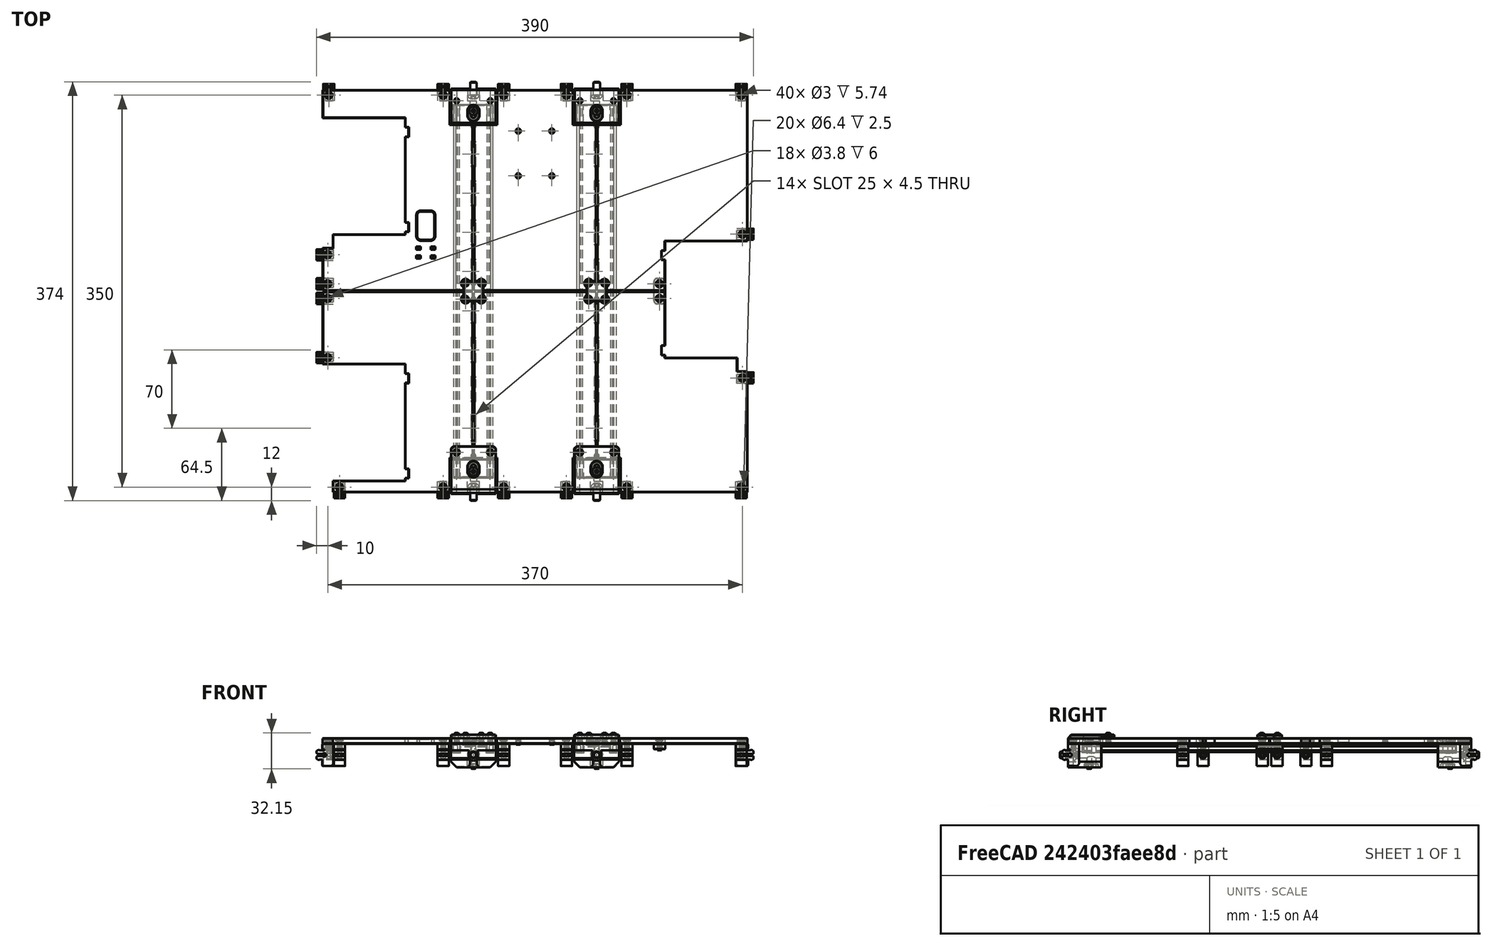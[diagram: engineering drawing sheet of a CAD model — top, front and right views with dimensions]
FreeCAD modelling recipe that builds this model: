
FCSTD DOCUMENT  (FreeCAD 0.19R24291 (Git))
Label: bottom-panel-250-assembly
License: Other
LicenseURL: GPL3
objects: Part::FeaturePython×84, Part::Feature×37, App::Part×5
note: 121 computed .brp shape members not serialized (recipe doc carries the construction recipe); baked Part::Feature solids carry a one-line shape summary decoded from their .brp

FEATURE [Part::Feature] Pocket003005  label="panel-mounter_D001"
  Placement = pos=(-179.5,-180,-10) rot=(0.57735,0.57735,0.57735;2.0944rad)
  shape: bbox 10 x 15 x 20 mm, 54 faces (baked)
FEATURE [Part::Feature] Pocket003006  label="panel-mounter_D002"
  Placement = pos=(-87,-180,-10) rot=(0.57735,0.57735,0.57735;2.0944rad)
  shape: bbox 10 x 15 x 20 mm, 54 faces (baked)
FEATURE [Part::Feature] Pocket003007  label="panel-mounter_D003"
  Placement = pos=(-33,-180,-10) rot=(0.57735,0.57735,0.57735;2.0944rad)
  shape: bbox 10 x 15 x 20 mm, 54 faces (baked)
FEATURE [Part::Feature] Pocket003008  label="panel-mounter_D004"
  Placement = pos=(23,-180,-10) rot=(0.57735,0.57735,0.57735;2.0944rad)
  shape: bbox 10 x 15 x 20 mm, 54 faces (baked)
FEATURE [Part::Feature] Pocket003009  label="panel-mounter_D005"
  Placement = pos=(77,-180,-10) rot=(0.57735,0.57735,0.57735;2.0944rad)
  shape: bbox 10 x 15 x 20 mm, 54 faces (baked)
FEATURE [Part::Feature] Pocket003010  label="panel-mounter_D006"
  Placement = pos=(179,-180,-10) rot=(0.57735,0.57735,0.57735;2.0944rad)
  shape: bbox 10 x 15 x 20 mm, 54 faces (baked)
FEATURE [Part::Feature] Pocket003011  label="panel-mounter_U001"
  Placement = pos=(-179,180,-10) rot=(0.57735,-0.57735,-0.57735;2.0944rad)
  shape: bbox 10 x 15 x 20 mm, 54 faces (baked)
FEATURE [Part::Feature] Pocket003012  label="panel-mounter_U002"
  Placement = pos=(-77,180,-10) rot=(0.57735,-0.57735,-0.57735;2.0944rad)
  shape: bbox 10 x 15 x 20 mm, 54 faces (baked)
FEATURE [Part::Feature] Pocket003013  label="panel-mounter_U003"
  Placement = pos=(-23,180,-10) rot=(0.57735,-0.57735,-0.57735;2.0944rad)
  shape: bbox 10 x 15 x 20 mm, 54 faces (baked)
FEATURE [Part::Feature] Pocket003014  label="panel-mounter_U004"
  Placement = pos=(33,180,-10) rot=(0.57735,-0.57735,-0.57735;2.0944rad)
  shape: bbox 10 x 15 x 20 mm, 54 faces (baked)
FEATURE [Part::Feature] Pocket003015  label="panel-mounter_U005"
  Placement = pos=(87,180,-10) rot=(0.57735,-0.57735,-0.57735;2.0944rad)
  shape: bbox 10 x 15 x 20 mm, 54 faces (baked)
FEATURE [Part::Feature] Pocket003016  label="panel-mounter_U006"
  Placement = pos=(189,180,-10) rot=(0.57735,-0.57735,-0.57735;2.0944rad)
  shape: bbox 10 x 15 x 20 mm, 54 faces (baked)
FEATURE [Part::Feature] Pocket003017  label="panel-mounter_L001"
  Placement = pos=(-190,37.4,-10) rot=(1,0,0;1.5708rad)
  shape: bbox 15 x 10 x 20 mm, 54 faces (baked)
FEATURE [Part::Feature] Pocket003018  label="panel-mounter_L002"
  Placement = pos=(-190,11.6,-10) rot=(1,0,0;1.5708rad)
  shape: bbox 15 x 10 x 20 mm, 54 faces (baked)
FEATURE [Part::Feature] Pocket003019  label="panel-mounter_L003"
  Placement = pos=(-190,-1.5,-10) rot=(1,0,0;1.5708rad)
  shape: bbox 15 x 10 x 20 mm, 54 faces (baked)
FEATURE [Part::Feature] Pocket003020  label="panel-mounter_L004"
  Placement = pos=(-190,-54.4,-10) rot=(1,0,0;1.5708rad)
  shape: bbox 15 x 10 x 20 mm, 54 faces (baked)
FEATURE [Part::Feature] Pocket003021  label="panel-mounter_R001"
  Placement = pos=(190,45.9,-10) rot=(0,0.707107,0.707107;3.14159rad)
  shape: bbox 15 x 10 x 20 mm, 54 faces (baked)
FEATURE [Part::Feature] Pocket003022  label="panel-mounter_R002"
  Placement = pos=(190,-82.5,-10) rot=(0,0.707107,0.707107;3.14159rad)
  shape: bbox 15 x 10 x 20 mm, 54 faces (baked)
FEATURE [Part::Feature] Cut002015026005020007004001  label="center-panel-connector"
  Placement = pos=(-55,0,5) rot=(0,0,1;0rad)
  shape: bbox 22 x 22 x 3 mm, 24 faces (baked)
FEATURE [Part::Feature] Cut002015026005020007004002  label="center-panel-connector001"
  Placement = pos=(55,0,5) rot=(0,0,1;0rad)
  shape: bbox 22 x 22 x 3 mm, 24 faces (baked)
FEATURE [Part::Feature] Chamfer003004002  label="bottom-din-holder"
  Placement = pos=(-55,-165,-25) rot=(0,0,1;3.14159rad)
  shape: bbox 40 x 31 x 21 mm, 75 faces (baked)
FEATURE [Part::Feature] Chamfer003004003  label="bottom-din-holder001"
  Placement = pos=(55,-165,-25) rot=(0,0,1;3.14159rad)
  shape: bbox 40 x 31 x 21 mm, 75 faces (baked)
FEATURE [Part::Feature] Chamfer003004004  label="bottom-din-holder002"
  Placement = pos=(55,165,-25) rot=(0,0,1;0rad)
  shape: bbox 40 x 31 x 21 mm, 75 faces (baked)
FEATURE [Part::Feature] Chamfer003004005  label="bottom-din-holder003"
  Placement = pos=(-55,165,-25) rot=(0,0,1;0rad)
  shape: bbox 40 x 31 x 21 mm, 75 faces (baked)
FEATURE [Part::Feature] Cut001001  label="front-din-cap"
  Placement = pos=(-55,-165,0) rot=(0,0,1;0rad)
  shape: bbox 40 x 41.5 x 9 mm, 50 faces (baked)
FEATURE [Part::Feature] Chamfer005007002029002004001  label="back-din-cap"
  Placement = pos=(-55,165,-25) rot=(0,0,1;0rad)
  shape: bbox 40 x 30 x 6 mm, 55 faces (baked)
FEATURE [Part::Feature] Chamfer005007002029002004002  label="back-din-cap001"
  Placement = pos=(55,165,-25) rot=(0,0,1;0rad)
  shape: bbox 40 x 30 x 6 mm, 55 faces (baked)
FEATURE [Part::Feature] Cut002015026005020007004003  label="front-din-cap001"
  Placement = pos=(55,-165,0) rot=(0,0,1;0rad)
  shape: bbox 40 x 41.5 x 9 mm, 50 faces (baked)
FEATURE [Part::Feature] Common001003002002003002  label="din-rail-332mm001"
  Placement = pos=(-17,53,20) rot=(0.707107,-0.707107,0;3.14159rad)
  shape: bbox 35 x 332 x 7.5 mm, 70 faces (baked)
FEATURE [Part::Feature] Common001003002002003003  label="din-rail-332mm002"
  Placement = pos=(93,53,20) rot=(0.707107,-0.707107,0;3.14159rad)
  shape: bbox 35 x 332 x 7.5 mm, 70 faces (baked)
FEATURE [Part::FeaturePython] Screw  label="M6x12-Screw004"  # Fasteners workbench fastener (typed FeaturePython)
  Placement = pos=(-55,-175,-10) rot=(-1,0,0;1.5708rad)
  baseObject = -> Chamfer003004002 [Edge49]
  diameter = 4
  invert = true
  length = 1
  lengthCustom = 12
  matchOuter = true
  offset = 0
  thread = false
  type = 40
FEATURE [Part::FeaturePython] Screw001  label="M6x12-Screw005"  # Fasteners workbench fastener (typed FeaturePython)
  Placement = pos=(55,-175,-10) rot=(-1,0,0;1.5708rad)
  baseObject = -> Chamfer003004003 [Edge49]
  diameter = 4
  invert = true
  length = 1
  lengthCustom = 12
  matchOuter = true
  offset = 0
  thread = false
  type = 40
FEATURE [Part::FeaturePython] Screw002  label="M6x12-Screw006"  # Fasteners workbench fastener (typed FeaturePython)
  Placement = pos=(55,175,-10) rot=(1,0,0;1.5708rad)
  baseObject = -> Chamfer003004004 [Edge49]
  diameter = 4
  invert = true
  length = 1
  lengthCustom = 12
  matchOuter = true
  offset = 0
  thread = false
  type = 40
FEATURE [Part::FeaturePython] Screw003  label="M6x12-Screw"  # Fasteners workbench fastener (typed FeaturePython)
  Placement = pos=(-55,175,-10) rot=(1,0,0;1.5708rad)
  baseObject = -> Chamfer003004005 [Edge49]
  diameter = 4
  invert = true
  length = 1
  lengthCustom = 12
  matchOuter = true
  offset = 0
  thread = false
  type = 40
FEATURE [Part::FeaturePython] Nut  label="M4-Nut"  # Fasteners workbench fastener (typed FeaturePython)
  Placement = pos=(-55,-161,-18) rot=(1,0,0;3.14159rad)
  baseObject = -> Chamfer003004002 [Edge141]
  diameter = 6
  invert = true
  matchOuter = true
  offset = 0
  thread = false
  type = 7
FEATURE [Part::FeaturePython] Nut001  label="M4-Nut004"  # Fasteners workbench fastener (typed FeaturePython)
  Placement = pos=(55,-161,-18) rot=(1,0,0;3.14159rad)
  baseObject = -> Chamfer003004003 [Edge141]
  diameter = 6
  invert = true
  matchOuter = true
  offset = 0
  thread = false
  type = 7
FEATURE [Part::FeaturePython] Nut002  label="M4-Nut005"  # Fasteners workbench fastener (typed FeaturePython)
  Placement = pos=(55,161,-18) rot=(1,0,0;3.14159rad)
  baseObject = -> Chamfer003004004 [Edge141]
  diameter = 6
  invert = true
  matchOuter = true
  offset = 0
  thread = false
  type = 7
FEATURE [Part::FeaturePython] Nut003  label="M4-Nut006"  # Fasteners workbench fastener (typed FeaturePython)
  Placement = pos=(-55,161,-18) rot=(1,0,0;3.14159rad)
  baseObject = -> Chamfer003004005 [Edge141]
  diameter = 6
  invert = true
  matchOuter = true
  offset = 0
  thread = false
  type = 7
FEATURE [Part::FeaturePython] Screw004  label="M4x25-Screw"  # Fasteners workbench fastener (typed FeaturePython)
  Placement = pos=(-55,161,2.5) rot=(0,0,1;0rad)
  baseObject = -> Chamfer005007002029002004001 [Edge49]
  diameter = 2
  invert = false
  length = 7
  lengthCustom = 25
  matchOuter = true
  offset = 0
  thread = false
  type = 40
FEATURE [Part::FeaturePython] Screw005  label="M4x25-Screw001"  # Fasteners workbench fastener (typed FeaturePython)
  Placement = pos=(55,161,2.5) rot=(0,0,1;0rad)
  baseObject = -> Chamfer005007002029002004002 [Edge49]
  diameter = 2
  invert = false
  length = 7
  lengthCustom = 25
  matchOuter = true
  offset = 0
  thread = false
  type = 40
FEATURE [Part::FeaturePython] Screw006  label="M4x25-Screw002"  # Fasteners workbench fastener (typed FeaturePython)
  Placement = pos=(55,-161,2.5) rot=(0,0,1;0rad)
  baseObject = -> Cut002015026005020007004003 [Edge118]
  diameter = 2
  invert = false
  length = 7
  lengthCustom = 25
  matchOuter = true
  offset = 0
  thread = false
  type = 40
FEATURE [Part::FeaturePython] Screw007  label="M4x25-Screw003"  # Fasteners workbench fastener (typed FeaturePython)
  Placement = pos=(-55,-161,2.5) rot=(0,0,1;0rad)
  baseObject = -> Cut001001 [Edge118]
  diameter = 2
  invert = false
  length = 7
  lengthCustom = 25
  matchOuter = true
  offset = 0
  thread = false
  type = 40
FEATURE [Part::FeaturePython] Screw008  label="M3x6-Screw"  # Fasteners workbench fastener (typed FeaturePython)
  Placement = pos=(70,-144,8) rot=(0,0,1;0rad)
  baseObject = -> Cut002015026005020007004003 [Edge45]
  diameter = 1
  invert = false
  length = 0
  lengthCustom = 6
  matchOuter = true
  offset = 0
  thread = false
  type = 40
FEATURE [Part::FeaturePython] Screw009  label="M3x6-Screw001"  # Fasteners workbench fastener (typed FeaturePython)
  Placement = pos=(40,-144,8) rot=(0,0,1;0rad)
  baseObject = -> Cut002015026005020007004003 [Edge44]
  diameter = 1
  invert = false
  length = 0
  lengthCustom = 6
  matchOuter = true
  offset = 0
  thread = false
  type = 40
FEATURE [Part::FeaturePython] Screw010  label="M3x6-Screw002"  # Fasteners workbench fastener (typed FeaturePython)
  Placement = pos=(-40,-144,8) rot=(0,0,1;0rad)
  baseObject = -> Cut001001 [Edge45]
  diameter = 1
  invert = false
  length = 0
  lengthCustom = 6
  matchOuter = true
  offset = 0
  thread = false
  type = 40
FEATURE [Part::FeaturePython] Screw011  label="M3x6-Screw003"  # Fasteners workbench fastener (typed FeaturePython)
  Placement = pos=(-70,-144,8) rot=(0,0,1;0rad)
  baseObject = -> Cut001001 [Edge44]
  diameter = 1
  invert = false
  length = 0
  lengthCustom = 6
  matchOuter = true
  offset = 0
  thread = false
  type = 40
FEATURE [Part::FeaturePython] HeatSet  label="M3x4-HeatSet"  # WARN: FeaturePython — macro-defined, semantics opaque (R4)
  Placement = pos=(70,170,5) rot=(0,0,1;0rad)
  baseObject = -> Chamfer005007002029002004002 [Edge114]
  diameter = 2
  invert = false
  offset = 0
FEATURE [Part::FeaturePython] HeatSet001  label="M3x4-HeatSet001"  # WARN: FeaturePython — macro-defined, semantics opaque (R4)
  Placement = pos=(40,170,5) rot=(0,0,1;0rad)
  baseObject = -> Chamfer005007002029002004002 [Edge88]
  diameter = 2
  invert = false
  offset = 0
FEATURE [Part::FeaturePython] Screw012  label="M3x6-Screw004"  # Fasteners workbench fastener (typed FeaturePython)
  Placement = pos=(62,7,8) rot=(0,0,1;0rad)
  baseObject = -> Cut002015026005020007004002 [Edge40]
  diameter = 1
  invert = false
  length = 0
  lengthCustom = 6
  matchOuter = true
  offset = 0
  thread = false
  type = 40
FEATURE [Part::FeaturePython] Screw013  label="M3x6-Screw005"  # Fasteners workbench fastener (typed FeaturePython)
  Placement = pos=(62,-7,8) rot=(0,0,1;0rad)
  baseObject = -> Cut002015026005020007004002 [Edge39]
  diameter = 1
  invert = false
  length = 0
  lengthCustom = 6
  matchOuter = true
  offset = 0
  thread = false
  type = 40
FEATURE [Part::FeaturePython] Screw014  label="M3x6-Screw006"  # Fasteners workbench fastener (typed FeaturePython)
  Placement = pos=(48,-7,8) rot=(0,0,1;0rad)
  baseObject = -> Cut002015026005020007004002 [Edge41]
  diameter = 1
  invert = false
  length = 0
  lengthCustom = 6
  matchOuter = true
  offset = 0
  thread = false
  type = 40
FEATURE [Part::FeaturePython] Screw015  label="M3x6-Screw007"  # Fasteners workbench fastener (typed FeaturePython)
  Placement = pos=(48,7,8) rot=(0,0,1;0rad)
  baseObject = -> Cut002015026005020007004002 [Edge42]
  diameter = 1
  invert = false
  length = 0
  lengthCustom = 6
  matchOuter = true
  offset = 0
  thread = false
  type = 40
FEATURE [Part::FeaturePython] Screw016  label="M3x6-Screw008"  # Fasteners workbench fastener (typed FeaturePython)
  Placement = pos=(-48,7,8) rot=(0,0,1;0rad)
  baseObject = -> Cut002015026005020007004001 [Edge40]
  diameter = 1
  invert = false
  length = 0
  lengthCustom = 6
  matchOuter = true
  offset = 0
  thread = false
  type = 40
FEATURE [Part::FeaturePython] Screw017  label="M3x6-Screw009"  # Fasteners workbench fastener (typed FeaturePython)
  Placement = pos=(-48,-7,8) rot=(0,0,1;0rad)
  baseObject = -> Cut002015026005020007004001 [Edge39]
  diameter = 1
  invert = false
  length = 0
  lengthCustom = 6
  matchOuter = true
  offset = 0
  thread = false
  type = 40
FEATURE [Part::FeaturePython] Screw018  label="M3x6-Screw010"  # Fasteners workbench fastener (typed FeaturePython)
  Placement = pos=(-62,-7,8) rot=(0,0,1;0rad)
  baseObject = -> Cut002015026005020007004001 [Edge41]
  diameter = 1
  invert = false
  length = 0
  lengthCustom = 6
  matchOuter = true
  offset = 0
  thread = false
  type = 40
FEATURE [Part::FeaturePython] Screw019  label="M3x6-Screw011"  # Fasteners workbench fastener (typed FeaturePython)
  Placement = pos=(-62,7,8) rot=(0,0,1;0rad)
  baseObject = -> Cut002015026005020007004001 [Edge42]
  diameter = 1
  invert = false
  length = 0
  lengthCustom = 6
  matchOuter = true
  offset = 0
  thread = false
  type = 40
FEATURE [Part::FeaturePython] HeatSet002  label="M3x4-HeatSet025"  # WARN: FeaturePython — macro-defined, semantics opaque (R4)
  Placement = pos=(184,175,1.8e-15) rot=(0,0,1;0rad)
  baseObject = -> Pocket003016 [Edge44]
  diameter = 2
  invert = false
  offset = 0
FEATURE [Part::FeaturePython] HeatSet003  label="M3x4-HeatSet026"  # WARN: FeaturePython — macro-defined, semantics opaque (R4)
  Placement = pos=(82,175,1.8e-15) rot=(0,0,1;0rad)
  baseObject = -> Pocket003015 [Edge44]
  diameter = 2
  invert = false
  offset = 0
FEATURE [Part::FeaturePython] HeatSet004  label="M3x4-HeatSet024"  # WARN: FeaturePython — macro-defined, semantics opaque (R4)
  Placement = pos=(28,175,1.8e-15) rot=(0,0,1;0rad)
  baseObject = -> Pocket003014 [Edge44]
  diameter = 2
  invert = false
  offset = 0
FEATURE [Part::FeaturePython] HeatSet005  label="M3x4-HeatSet028"  # WARN: FeaturePython — macro-defined, semantics opaque (R4)
  Placement = pos=(-28,175,1.8e-15) rot=(0,0,1;0rad)
  baseObject = -> Pocket003013 [Edge44]
  diameter = 2
  invert = false
  offset = 0
FEATURE [Part::FeaturePython] HeatSet006  label="M3x4-HeatSet018"  # WARN: FeaturePython — macro-defined, semantics opaque (R4)
  Placement = pos=(-82,175,1.8e-15) rot=(0,0,1;0rad)
  baseObject = -> Pocket003012 [Edge44]
  diameter = 2
  invert = false
  offset = 0
FEATURE [Part::FeaturePython] HeatSet007  label="M3x4-HeatSet017"  # WARN: FeaturePython — macro-defined, semantics opaque (R4)
  Placement = pos=(-184,175,1.8e-15) rot=(0,0,1;0rad)
  baseObject = -> Pocket003011 [Edge44]
  diameter = 2
  invert = false
  offset = 0
FEATURE [Part::FeaturePython] HeatSet008  label="M3x4-HeatSet016"  # WARN: FeaturePython — macro-defined, semantics opaque (R4)
  Placement = pos=(-185,32.4,-7.1e-15) rot=(0,0,1;0rad)
  baseObject = -> Pocket003017 [Edge44]
  diameter = 2
  invert = false
  offset = 0
FEATURE [Part::FeaturePython] HeatSet009  label="M3x4-HeatSet023"  # WARN: FeaturePython — macro-defined, semantics opaque (R4)
  Placement = pos=(-185,6.6,-1.8e-15) rot=(0,0,1;0rad)
  baseObject = -> Pocket003018 [Edge44]
  diameter = 2
  invert = false
  offset = 0
FEATURE [Part::FeaturePython] HeatSet010  label="M3x4-HeatSet014"  # WARN: FeaturePython — macro-defined, semantics opaque (R4)
  Placement = pos=(-185,-6.5,2e-15) rot=(0,0,1;0rad)
  baseObject = -> Pocket003019 [Edge44]
  diameter = 2
  invert = false
  offset = 0
FEATURE [Part::FeaturePython] HeatSet011  label="M3x4-HeatSet013"  # WARN: FeaturePython — macro-defined, semantics opaque (R4)
  Placement = pos=(-185,-59.4,1.2e-14) rot=(0,0,1;0rad)
  baseObject = -> Pocket003020 [Edge44]
  diameter = 2
  invert = false
  offset = 0
FEATURE [Part::FeaturePython] HeatSet012  label="M3x4-HeatSet012"  # WARN: FeaturePython — macro-defined, semantics opaque (R4)
  Placement = pos=(-174.5,-175,3.91e-14) rot=(0,0,1;0rad)
  baseObject = -> Pocket003005 [Edge44]
  diameter = 2
  invert = false
  offset = 0
FEATURE [Part::FeaturePython] HeatSet013  label="M3x4-HeatSet011"  # WARN: FeaturePython — macro-defined, semantics opaque (R4)
  Placement = pos=(-82,-175,3.91e-14) rot=(0,0,1;0rad)
  baseObject = -> Pocket003006 [Edge44]
  diameter = 2
  invert = false
  offset = 0
FEATURE [Part::FeaturePython] HeatSet014  label="M3x4-HeatSet027"  # WARN: FeaturePython — macro-defined, semantics opaque (R4)
  Placement = pos=(-28,-175,3.91e-14) rot=(0,0,1;0rad)
  baseObject = -> Pocket003007 [Edge44]
  diameter = 2
  invert = false
  offset = 0
FEATURE [Part::FeaturePython] HeatSet015  label="M3x4-HeatSet020"  # WARN: FeaturePython — macro-defined, semantics opaque (R4)
  Placement = pos=(28,-175,3.91e-14) rot=(0,0,1;0rad)
  baseObject = -> Pocket003008 [Edge44]
  diameter = 2
  invert = false
  offset = 0
FEATURE [Part::FeaturePython] HeatSet016  label="M3x4-HeatSet021"  # WARN: FeaturePython — macro-defined, semantics opaque (R4)
  Placement = pos=(82,-175,3.91e-14) rot=(0,0,1;0rad)
  baseObject = -> Pocket003009 [Edge44]
  diameter = 2
  invert = false
  offset = 0
FEATURE [Part::FeaturePython] HeatSet017  label="M3x4-HeatSet022"  # WARN: FeaturePython — macro-defined, semantics opaque (R4)
  Placement = pos=(184,-175,3.91e-14) rot=(0,0,1;0rad)
  baseObject = -> Pocket003010 [Edge44]
  diameter = 2
  invert = false
  offset = 0
FEATURE [Part::FeaturePython] HeatSet018  label="M3x4-HeatSet019"  # WARN: FeaturePython — macro-defined, semantics opaque (R4)
  Placement = pos=(185,-77.5,1.49e-14) rot=(0,0,1;0rad)
  baseObject = -> Pocket003022 [Edge44]
  diameter = 2
  invert = false
  offset = 0
FEATURE [Part::FeaturePython] HeatSet019  label="M3x4-HeatSet015"  # WARN: FeaturePython — macro-defined, semantics opaque (R4)
  Placement = pos=(185,50.9,-1.4e-14) rot=(0,0,1;0rad)
  baseObject = -> Pocket003021 [Edge44]
  diameter = 2
  invert = false
  offset = 0
FEATURE [App::Part] Part003  label="panel-mounter"
  Group = -> [Pocket003005,Pocket003006,Pocket003007,Pocket003008,Pocket003009,Pocket003010,Pocket003011,Pocket003012,Pocket003013,Pocket003014,Pocket003015,Pocket003016,Pocket003017,Pocket003018,Pocket003019,Pocket003020,Pocket003021,Pocket003022,HeatSet013,HeatSet012,HeatSet011,HeatSet010,HeatSet019,HeatSet008,HeatSet007,HeatSet006,HeatSet018,HeatSet015,HeatSet016,HeatSet017,HeatSet009,HeatSet004,HeatSet002,+3 more]
  Origin = -> Origin003
FEATURE [Part::FeaturePython] HeatSet020  label="M3x4-HeatSet029"  # WARN: FeaturePython — macro-defined, semantics opaque (R4)
  Placement = pos=(15,143,5) rot=(0,0,1;0rad)
  diameter = 2
  invert = false
  offset = 0
FEATURE [Part::FeaturePython] HeatSet021  label="M3x4-HeatSet030"  # WARN: FeaturePython — macro-defined, semantics opaque (R4)
  Placement = pos=(15,103,5) rot=(0,0,1;0rad)
  diameter = 2
  invert = false
  offset = 0
FEATURE [Part::FeaturePython] HeatSet022  label="M3x4-HeatSet031"  # WARN: FeaturePython — macro-defined, semantics opaque (R4)
  Placement = pos=(-15,103,5) rot=(0,0,1;0rad)
  diameter = 2
  invert = false
  offset = 0
FEATURE [Part::FeaturePython] HeatSet023  label="M3x4-HeatSet032"  # WARN: FeaturePython — macro-defined, semantics opaque (R4)
  Placement = pos=(-15,143,5) rot=(0,0,1;0rad)
  diameter = 2
  invert = false
  offset = 0
FEATURE [Part::FeaturePython] HeatSet024  label="M3x4-HeatSet033"  # WARN: FeaturePython — macro-defined, semantics opaque (R4)
  Placement = pos=(-48,7,5) rot=(0,0,1;0rad)
  diameter = 2
  invert = false
  offset = 0
FEATURE [Part::FeaturePython] HeatSet025  label="M3x4-HeatSet034"  # WARN: FeaturePython — macro-defined, semantics opaque (R4)
  Placement = pos=(48,7,5) rot=(0,0,1;0rad)
  diameter = 2
  invert = false
  offset = 0
FEATURE [Part::FeaturePython] HeatSet026  label="M3x4-HeatSet035"  # WARN: FeaturePython — macro-defined, semantics opaque (R4)
  Placement = pos=(-48,-7,5) rot=(0,0,1;0rad)
  diameter = 2
  invert = false
  offset = 0
FEATURE [Part::FeaturePython] HeatSet027  label="M3x4-HeatSet036"  # WARN: FeaturePython — macro-defined, semantics opaque (R4)
  Placement = pos=(48,-7,5) rot=(0,0,1;0rad)
  diameter = 2
  invert = false
  offset = 0
FEATURE [Part::FeaturePython] HeatSet028  label="M3x4-HeatSet037"  # WARN: FeaturePython — macro-defined, semantics opaque (R4)
  Placement = pos=(40,-144,5) rot=(0,0,1;0rad)
  diameter = 2
  invert = false
  offset = 0
FEATURE [Part::FeaturePython] HeatSet029  label="M3x4-HeatSet038"  # WARN: FeaturePython — macro-defined, semantics opaque (R4)
  Placement = pos=(-40,-144,5) rot=(0,0,1;0rad)
  diameter = 2
  invert = false
  offset = 0
FEATURE [Part::FeaturePython] HeatSet030  label="M3x4-HeatSet039"  # WARN: FeaturePython — macro-defined, semantics opaque (R4)
  Placement = pos=(-62,-7,5) rot=(0,0,1;0rad)
  diameter = 2
  invert = false
  offset = 0
FEATURE [Part::FeaturePython] HeatSet031  label="M3x4-HeatSet040"  # WARN: FeaturePython — macro-defined, semantics opaque (R4)
  Placement = pos=(-70,-144,5) rot=(0,0,1;0rad)
  diameter = 2
  invert = false
  offset = 0
FEATURE [Part::FeaturePython] HeatSet032  label="M3x4-HeatSet041"  # WARN: FeaturePython — macro-defined, semantics opaque (R4)
  Placement = pos=(-62,7,5) rot=(0,0,1;0rad)
  diameter = 2
  invert = false
  offset = 0
FEATURE [Part::FeaturePython] HeatSet033  label="M3x4-HeatSet042"  # WARN: FeaturePython — macro-defined, semantics opaque (R4)
  Placement = pos=(62,-7,5) rot=(0,0,1;0rad)
  diameter = 2
  invert = false
  offset = 0
FEATURE [Part::FeaturePython] HeatSet034  label="M3x4-HeatSet043"  # WARN: FeaturePython — macro-defined, semantics opaque (R4)
  Placement = pos=(70,-144,5) rot=(0,0,1;0rad)
  diameter = 2
  invert = false
  offset = 0
FEATURE [Part::FeaturePython] HeatSet035  label="M3x4-HeatSet044"  # WARN: FeaturePython — macro-defined, semantics opaque (R4)
  Placement = pos=(62,7,5) rot=(0,0,1;0rad)
  diameter = 2
  invert = false
  offset = 0
FEATURE [Part::FeaturePython] Screw020  label="M3x6-Screw029"  # Fasteners workbench fastener (typed FeaturePython)
  Placement = pos=(185,50.94,2.5) rot=(0,0,1;0rad)
  diameter = 1
  invert = false
  length = 0
  lengthCustom = 6
  matchOuter = true
  offset = 0
  thread = false
  type = 40
FEATURE [Part::FeaturePython] Screw021  label="M3x6-Screw030"  # Fasteners workbench fastener (typed FeaturePython)
  Placement = pos=(184,175,2.5) rot=(0,0,1;0rad)
  diameter = 1
  invert = false
  length = 0
  lengthCustom = 6
  matchOuter = true
  offset = 0
  thread = false
  type = 40
FEATURE [Part::FeaturePython] Screw022  label="M3x6-Screw031"  # Fasteners workbench fastener (typed FeaturePython)
  Placement = pos=(82,175,2.5) rot=(0,0,1;0rad)
  diameter = 1
  invert = false
  length = 0
  lengthCustom = 6
  matchOuter = true
  offset = 0
  thread = false
  type = 40
FEATURE [Part::FeaturePython] Screw023  label="M3x6-Screw032"  # Fasteners workbench fastener (typed FeaturePython)
  Placement = pos=(28,175,2.5) rot=(0,0,1;0rad)
  diameter = 1
  invert = false
  length = 0
  lengthCustom = 6
  matchOuter = true
  offset = 0
  thread = false
  type = 40
FEATURE [Part::FeaturePython] Screw024  label="M3x6-Screw033"  # Fasteners workbench fastener (typed FeaturePython)
  Placement = pos=(-28,175,2.5) rot=(0,0,1;0rad)
  diameter = 1
  invert = false
  length = 0
  lengthCustom = 6
  matchOuter = true
  offset = 0
  thread = false
  type = 40
FEATURE [Part::FeaturePython] Screw025  label="M3x6-Screw034"  # Fasteners workbench fastener (typed FeaturePython)
  Placement = pos=(-82,175,2.5) rot=(0,0,1;0rad)
  diameter = 1
  invert = false
  length = 0
  lengthCustom = 6
  matchOuter = true
  offset = 0
  thread = false
  type = 40
FEATURE [Part::FeaturePython] Screw026  label="M3x6-Screw035"  # Fasteners workbench fastener (typed FeaturePython)
  Placement = pos=(-184,175,2.5) rot=(0,0,1;0rad)
  diameter = 1
  invert = false
  length = 0
  lengthCustom = 6
  matchOuter = true
  offset = 0
  thread = false
  type = 40
FEATURE [Part::FeaturePython] Screw027  label="M3x6-Screw036"  # Fasteners workbench fastener (typed FeaturePython)
  Placement = pos=(-185,32.5,2.5) rot=(0,0,1;0rad)
  diameter = 1
  invert = false
  length = 0
  lengthCustom = 6
  matchOuter = true
  offset = 0
  thread = false
  type = 40
FEATURE [Part::FeaturePython] Screw028  label="M3x6-Screw042"  # Fasteners workbench fastener (typed FeaturePython)
  Placement = pos=(-185,-6.5,2.5) rot=(0,0,1;0rad)
  diameter = 1
  invert = false
  length = 0
  lengthCustom = 6
  matchOuter = true
  offset = 0
  thread = false
  type = 40
FEATURE [Part::FeaturePython] Screw029  label="M3x6-Screw043"  # Fasteners workbench fastener (typed FeaturePython)
  Placement = pos=(-185,-59.36,2.5) rot=(0,0,1;0rad)
  diameter = 1
  invert = false
  length = 0
  lengthCustom = 6
  matchOuter = true
  offset = 0
  thread = false
  type = 40
FEATURE [Part::FeaturePython] Screw030  label="M3x6-Screw044"  # Fasteners workbench fastener (typed FeaturePython)
  Placement = pos=(-174.5,-175,2.5) rot=(0,0,1;0rad)
  diameter = 1
  invert = false
  length = 0
  lengthCustom = 6
  matchOuter = true
  offset = 0
  thread = false
  type = 40
FEATURE [Part::FeaturePython] Screw031  label="M3x6-Screw045"  # Fasteners workbench fastener (typed FeaturePython)
  Placement = pos=(-82,-175,2.5) rot=(0,0,1;0rad)
  diameter = 1
  invert = false
  length = 0
  lengthCustom = 6
  matchOuter = true
  offset = 0
  thread = false
  type = 40
FEATURE [Part::FeaturePython] Screw032  label="M3x6-Screw040"  # Fasteners workbench fastener (typed FeaturePython)
  Placement = pos=(28,-175,2.5) rot=(0,0,1;0rad)
  diameter = 1
  invert = false
  length = 0
  lengthCustom = 6
  matchOuter = true
  offset = 0
  thread = false
  type = 40
FEATURE [Part::FeaturePython] Screw033  label="M3x6-Screw041"  # Fasteners workbench fastener (typed FeaturePython)
  Placement = pos=(-28,-175,2.5) rot=(0,0,1;0rad)
  diameter = 1
  invert = false
  length = 0
  lengthCustom = 6
  matchOuter = true
  offset = 0
  thread = false
  type = 40
FEATURE [Part::FeaturePython] Screw034  label="M3x6-Screw037"  # Fasteners workbench fastener (typed FeaturePython)
  Placement = pos=(184,-175,2.5) rot=(0,0,1;0rad)
  diameter = 1
  invert = false
  length = 0
  lengthCustom = 6
  matchOuter = true
  offset = 0
  thread = false
  type = 40
FEATURE [Part::FeaturePython] Screw035  label="M3x6-Screw038"  # Fasteners workbench fastener (typed FeaturePython)
  Placement = pos=(82,-175,2.5) rot=(0,0,1;0rad)
  diameter = 1
  invert = false
  length = 0
  lengthCustom = 6
  matchOuter = true
  offset = 0
  thread = false
  type = 40
FEATURE [Part::FeaturePython] Screw036  label="M3x6-Screw039"  # Fasteners workbench fastener (typed FeaturePython)
  Placement = pos=(185,-77.5,2.5) rot=(0,0,1;0rad)
  diameter = 1
  invert = false
  length = 0
  lengthCustom = 6
  matchOuter = true
  offset = 0
  thread = false
  type = 40
FEATURE [Part::Feature] Chamfer007  label="panel-side-connector"
  Placement = pos=(111,0,-5) rot=(0,0,1;0rad)
  shape: bbox 10 x 23 x 5 mm, 32 faces (baked)
FEATURE [Part::Feature] Chamfer001001  label="panel-BL"
  shape: bbox 134 x 179 x 5 mm, 131 faces (baked)
FEATURE [Part::Feature] Chamfer002001  label="panel-FL"
  shape: bbox 134 x 179 x 5 mm, 78 faces (baked)
FEATURE [Part::Feature] Chamfer003001  label="panel-FC"
  shape: bbox 109 x 179 x 5 mm, 46 faces (baked)
FEATURE [Part::Feature] Chamfer004001  label="panel-FR"
  shape: bbox 134 x 179 x 5 mm, 66 faces (baked)
FEATURE [Part::Feature] Chamfer005001  label="panel-BR"
  shape: bbox 134 x 179 x 5 mm, 57 faces (baked)
FEATURE [Part::Feature] Chamfer006001  label="panel-BC"
  shape: bbox 109 x 179 x 5 mm, 52 faces (baked)
FEATURE [Part::FeaturePython] Screw037  label="M3x6-Screw046"  # Fasteners workbench fastener (typed FeaturePython)
  Placement = pos=(-185,6.5,2.5) rot=(0,0,1;0rad)
  baseObject = -> Chamfer001001 [Edge126]
  diameter = 1
  invert = false
  length = 0
  lengthCustom = 6
  matchOuter = true
  offset = 0
  thread = false
  type = 40
FEATURE [Part::FeaturePython] Screw038  label="M3x6-Screw047"  # Fasteners workbench fastener (typed FeaturePython)
  Placement = pos=(111,6.5,2.5) rot=(0,0,1;0rad)
  baseObject = -> Chamfer005001 [Edge76]
  diameter = 1
  invert = false
  length = 0
  lengthCustom = 6
  matchOuter = true
  offset = 0
  thread = false
  type = 40
FEATURE [Part::FeaturePython] Screw039  label="M3x6-Screw048"  # Fasteners workbench fastener (typed FeaturePython)
  Placement = pos=(111,-6.5,2.5) rot=(0,0,1;0rad)
  baseObject = -> Chamfer004001 [Edge92]
  diameter = 1
  invert = false
  length = 0
  lengthCustom = 6
  matchOuter = true
  offset = 0
  thread = false
  type = 40
FEATURE [App::Part] Part001  label="panel"
  Group = -> [HeatSet020,HeatSet021,HeatSet022,HeatSet023,HeatSet024,HeatSet025,HeatSet026,HeatSet027,HeatSet028,HeatSet029,HeatSet030,HeatSet031,HeatSet032,HeatSet033,HeatSet034,HeatSet035,Screw020,Screw021,Screw022,Screw023,Screw024,Screw025,Screw026,Screw027,Screw028,Screw029,Screw030,Screw031,Screw032,Screw033,Screw034,Screw035,Screw036,Chamfer001001,Chamfer002001,Chamfer003001,Chamfer004001,Chamfer005001,+4 more]
  Origin = -> Origin001
FEATURE [Part::FeaturePython] HeatSet036  label="M3x4-HeatSet045"  # WARN: FeaturePython — macro-defined, semantics opaque (R4)
  Placement = pos=(111,-6.5,0) rot=(0,0,1;0rad)
  baseObject = -> Chamfer007 [Edge39]
  diameter = 2
  invert = false
  offset = 0
FEATURE [Part::FeaturePython] HeatSet037  label="M3-HeatSet001"  # WARN: FeaturePython — macro-defined, semantics opaque (R4)
  Placement = pos=(111,6.5,0) rot=(0,0,1;0rad)
  baseObject = -> Chamfer007 [Edge40]
  diameter = 2
  invert = false
  offset = 0
FEATURE [App::Part] Part002  label="panel-connector"
  Group = -> [Cut002015026005020007004002,Cut002015026005020007004001,Screw012,Screw013,Screw014,Screw015,Screw016,Screw017,Screw018,Screw019,Chamfer007,HeatSet036,HeatSet037]
  Origin = -> Origin002
FEATURE [Part::FeaturePython] HeatSet038  label="M3x4-HeatSet046"  # WARN: FeaturePython — macro-defined, semantics opaque (R4)
  Placement = pos=(-70,170,5) rot=(0,0,1;0rad)
  baseObject = -> Chamfer005007002029002004001 [Edge88]
  diameter = 2
  invert = false
  offset = 0
FEATURE [Part::FeaturePython] HeatSet039  label="M3x4-HeatSet002"  # WARN: FeaturePython — macro-defined, semantics opaque (R4)
  Placement = pos=(-40,170,5) rot=(0,0,1;0rad)
  baseObject = -> Chamfer005007002029002004001 [Edge114]
  diameter = 2
  invert = false
  offset = 0
FEATURE [App::Part] Part  label="bottom-din"
  Group = -> [Common001003002002003003,Common001003002002003002,Cut001001,Chamfer005007002029002004001,Chamfer005007002029002004002,Cut002015026005020007004003,Chamfer003004002,Chamfer003004003,Chamfer003004004,Chamfer003004005,Screw003,Screw,Screw001,Screw002,Nut,Nut001,Nut002,Nut003,Screw004,Screw005,Screw006,Screw007,Screw008,Screw009,Screw010,Screw011,HeatSet001,HeatSet,HeatSet039,HeatSet038]
  Origin = -> Origin
FEATURE [App::Part] Part004  label="bottom-panel"
  Group = -> [Part,Part001,Part002,Part003]
  Origin = -> Origin004
